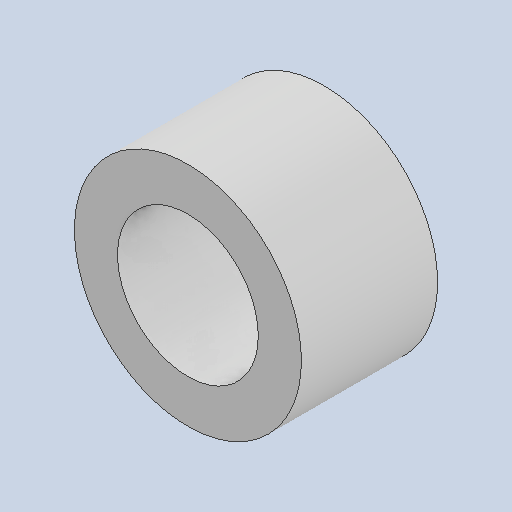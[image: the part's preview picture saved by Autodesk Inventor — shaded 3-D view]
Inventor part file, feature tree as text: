
AUTODESK INVENTOR PART (.ipt)
format: ipt  version: 2023 (Build 270158000, 158)  size: 143,360 bytes
history: native  units: in
note: dims shown in document units (in); Inventor stores cm internally (conversion verified against a paired STEP export)
features: extrude x1, sketch x1
ambient origin geometry x8: Origin, YZ Plane, XZ Plane, XY Plane, X Axis, Y Axis, Z Axis, Center Point
bodies: Solid1 (feature_tree)
feature tree (2):
  extrude  "Extrusion1"  Depth=0.3937in
  sketch  "Sketch1"  dims[d0=0.2441in d1=0.3937in d2=0.2362in d3=0.0in]
